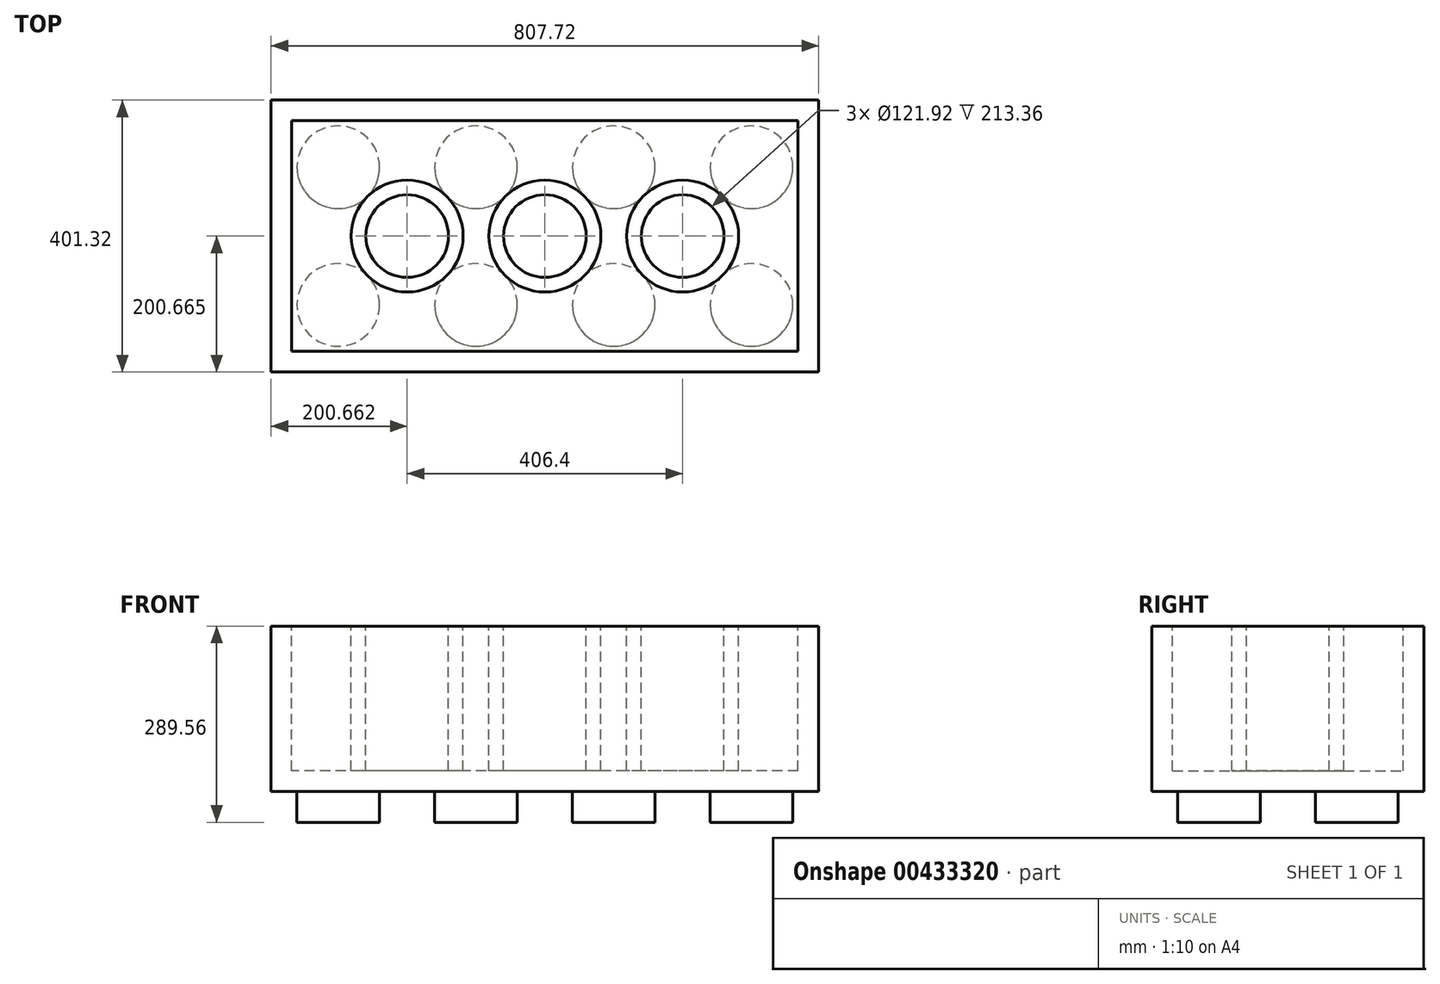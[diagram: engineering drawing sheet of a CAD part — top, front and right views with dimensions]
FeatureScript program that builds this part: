
annotation { "Feature Type Name" : "Feature", "Feature Type Description" : "" }
export const myFeature = defineFeature(function(context is Context, id is Id, definition is map)
    precondition{}
    {
        {
            var Q0;
            Q0=qCreatedBy(makeId("Top.planeOp"),FACE);
            var sketch = newSketch(context, id + "F0", { "sketchPlane" : qUnion([Q0])});
            skLineSegment(sketch, "E0.bottom", {"start": v(-378.63, 186) * mm, "end": v(429.1, 186) * mm});
            skLineSegment(sketch, "E0.top", {"start": v(-378.63, -215.32) * mm, "end": v(429.1, -215.32) * mm});
            skLineSegment(sketch, "E0.left", {"start": v(-378.63, 186) * mm, "end": v(-378.63, -215.32) * mm});
            skLineSegment(sketch, "E0.right", {"start": v(429.1, 186) * mm, "end": v(429.1, -215.32) * mm});
            skSolve(sketch);
        }
        {
            var Q0;
            Q0=makeQuery(id+"F0.imprint","IMPRINT",FACE,{"disambiguationData":[TD([[makeQuery(id+"F0.imprint","IMPRINT",EDGE,{"derivedFrom":sQuery(id+"F0.wireOp",EDGE,"E0.bottom")}),-1.0]])]});
            extrude(context, id + "F1", {"entities" : qUnion([Q0]), "oppositeDirection" : true, "depth" : 243.84 * mm});
        }
        {
            var Q0;
            Q0=makeQuery(id+"F1.opExtrude","CAP_FACE",FACE,{"disambiguationData":[OSD([sQuery(id+"F0.wireOp",EDGE,"E0.bottom"),sQuery(id+"F0.wireOp",EDGE,"E0.top"),sQuery(id+"F0.wireOp",EDGE,"E0.left"),sQuery(id+"F0.wireOp",EDGE,"E0.right")])],"isStart":false});
            var sketch = newSketch(context, id + "F2", { "sketchPlane" : qUnion([Q0])});
            skCircle(sketch, "E1", {"center": v(-279.57, 116.26) * mm, "radius": 60.96 * mm});
            skCircle(sketch, "E2.0.1.0", {"center": v(-279.57, -86.94) * mm, "radius": 60.96 * mm});
            skCircle(sketch, "E2.1.0.0", {"center": v(-76.37, 116.26) * mm, "radius": 60.96 * mm});
            skCircle(sketch, "E2.1.1.0", {"center": v(-76.37, -86.94) * mm, "radius": 60.96 * mm});
            skCircle(sketch, "E2.2.0.0", {"center": v(126.83, 116.26) * mm, "radius": 60.96 * mm});
            skCircle(sketch, "E2.2.1.0", {"center": v(126.83, -86.94) * mm, "radius": 60.96 * mm});
            skCircle(sketch, "E2.3.0.0", {"center": v(330.03, 116.26) * mm, "radius": 60.96 * mm});
            skCircle(sketch, "E2.3.1.0", {"center": v(330.03, -86.94) * mm, "radius": 60.96 * mm});
            skLineSegment(sketch, "E2.direction1", {"start": v(-279.57, 116.26) * mm, "end": v(-76.37, 116.26) * mm, "construction": true});
            skLineSegment(sketch, "E2.direction2", {"start": v(-279.57, 116.26) * mm, "end": v(-279.57, -86.94) * mm, "construction": true});
            skSolve(sketch);
        }
        {
            var Q0;
            Q0 = qSketchRegion(id + "F2", true);
            extrude(context, id + "F3", {"entities" : qUnion([Q0]), "operationType" : NewBodyOperationType.ADD, "depth" : 45.72 * mm});
        }
        {
            var Q0;
            Q0=makeQuery(id+"F1.opExtrude","CAP_FACE",FACE,{"disambiguationData":[OSD([sQuery(id+"F0.wireOp",EDGE,"E0.bottom"),sQuery(id+"F0.wireOp",EDGE,"E0.top"),sQuery(id+"F0.wireOp",EDGE,"E0.left"),sQuery(id+"F0.wireOp",EDGE,"E0.right")])],"isStart":true});
            var sketch = newSketch(context, id + "F4", { "sketchPlane" : qUnion([Q0])});
            skCircle(sketch, "E3", {"center": v(-177.97, -14.66) * mm, "radius": 82.55 * mm});
            skCircle(sketch, "E4", {"center": v(-177.97, -14.66) * mm, "radius": 60.96 * mm});
            skCircle(sketch, "E5.1.0.0", {"center": v(25.23, -14.66) * mm, "radius": 60.96 * mm});
            skCircle(sketch, "E5.1.0.1", {"center": v(25.23, -14.66) * mm, "radius": 82.55 * mm});
            skCircle(sketch, "E5.2.0.0", {"center": v(228.43, -14.66) * mm, "radius": 60.96 * mm});
            skCircle(sketch, "E5.2.0.1", {"center": v(228.43, -14.66) * mm, "radius": 82.55 * mm});
            skLineSegment(sketch, "E5.direction1", {"start": v(-177.97, -14.66) * mm, "end": v(25.23, -14.66) * mm, "construction": true});
            skSolve(sketch);
        }
        {
            var Q0;
            Q0=makeQuery(id+"F4.imprint","IMPRINT",FACE,{"disambiguationData":[TD([[makeQuery(id+"F4.imprint","IMPRINT",EDGE,{"derivedFrom":sQuery(id+"F4.wireOp",EDGE,"E3")}),-1.0]])]});
            var sketch = newSketch(context, id + "F5", { "sketchPlane" : qUnion([Q0])});
            skLineSegment(sketch, "E6.bottom", {"start": v(-348.15, 155.52) * mm, "end": v(398.61, 155.52) * mm});
            skLineSegment(sketch, "E6.top", {"start": v(-348.15, -184.84) * mm, "end": v(398.61, -184.84) * mm});
            skLineSegment(sketch, "E6.left", {"start": v(-348.15, 155.52) * mm, "end": v(-348.15, -184.84) * mm});
            skLineSegment(sketch, "E6.right", {"start": v(398.61, 155.52) * mm, "end": v(398.61, -184.84) * mm});
            skSolve(sketch);
        }
        {
            var Q0;
            Q0 = qSketchRegion(id + "F5", true);
            extrude(context, id + "F6", {"entities" : qUnion([Q0]), "operationType" : NewBodyOperationType.ADD, "oppositeDirection" : true, "depth" : 213.36 * mm});
        }
        {
            var Q0;
            Q0=makeQuery(id+"F4.imprint","IMPRINT",FACE,{"disambiguationData":[TD([[makeQuery(id+"F4.imprint","IMPRINT",EDGE,{"derivedFrom":sQuery(id+"F4.wireOp",EDGE,"E3")}),-1.0]])]});
            var sketch = newSketch(context, id + "F7", { "sketchPlane" : qUnion([Q0])});
            skLineSegment(sketch, "E7.bottom", {"start": v(398.61, -184.84) * mm, "end": v(-348.15, -184.84) * mm});
            skLineSegment(sketch, "E7.top", {"start": v(398.61, 155.52) * mm, "end": v(-348.15, 155.52) * mm});
            skLineSegment(sketch, "E7.left", {"start": v(398.61, -184.84) * mm, "end": v(398.61, 155.52) * mm});
            skLineSegment(sketch, "E7.right", {"start": v(-348.15, -184.84) * mm, "end": v(-348.15, 155.52) * mm});
            skSolve(sketch);
        }
        {
            var Q0;
            Q0=makeQuery(id+"F7.imprint","IMPRINT",FACE,{"disambiguationData":[TD([[makeQuery(id+"F7.imprint","IMPRINT",EDGE,{"derivedFrom":sQuery(id+"F7.wireOp",EDGE,"E7.bottom")}),-1.0]])]});
            var Q1;
            Q1=makeQuery(id+"F4.imprint","IMPRINT",FACE,{"disambiguationData":[TD([[makeQuery(id+"F4.imprint","IMPRINT",EDGE,{"derivedFrom":sQuery(id+"F4.wireOp",EDGE,"E5.2.0.0")}),1.0]])]});
            var Q2;
            Q2=makeQuery(id+"F4.imprint","IMPRINT",FACE,{"disambiguationData":[TD([[makeQuery(id+"F4.imprint","IMPRINT",EDGE,{"derivedFrom":sQuery(id+"F4.wireOp",EDGE,"E4")}),1.0]])]});
            var Q3;
            Q3=makeQuery(id+"F4.imprint","IMPRINT",FACE,{"disambiguationData":[TD([[makeQuery(id+"F4.imprint","IMPRINT",EDGE,{"derivedFrom":sQuery(id+"F4.wireOp",EDGE,"E5.1.0.0")}),1.0]])]});
            extrude(context, id + "F8", {"entities" : qUnion([Q0, Q1, Q2, Q3]), "operationType" : NewBodyOperationType.REMOVE, "oppositeDirection" : true, "depth" : 213.36 * mm});
        }
    });
